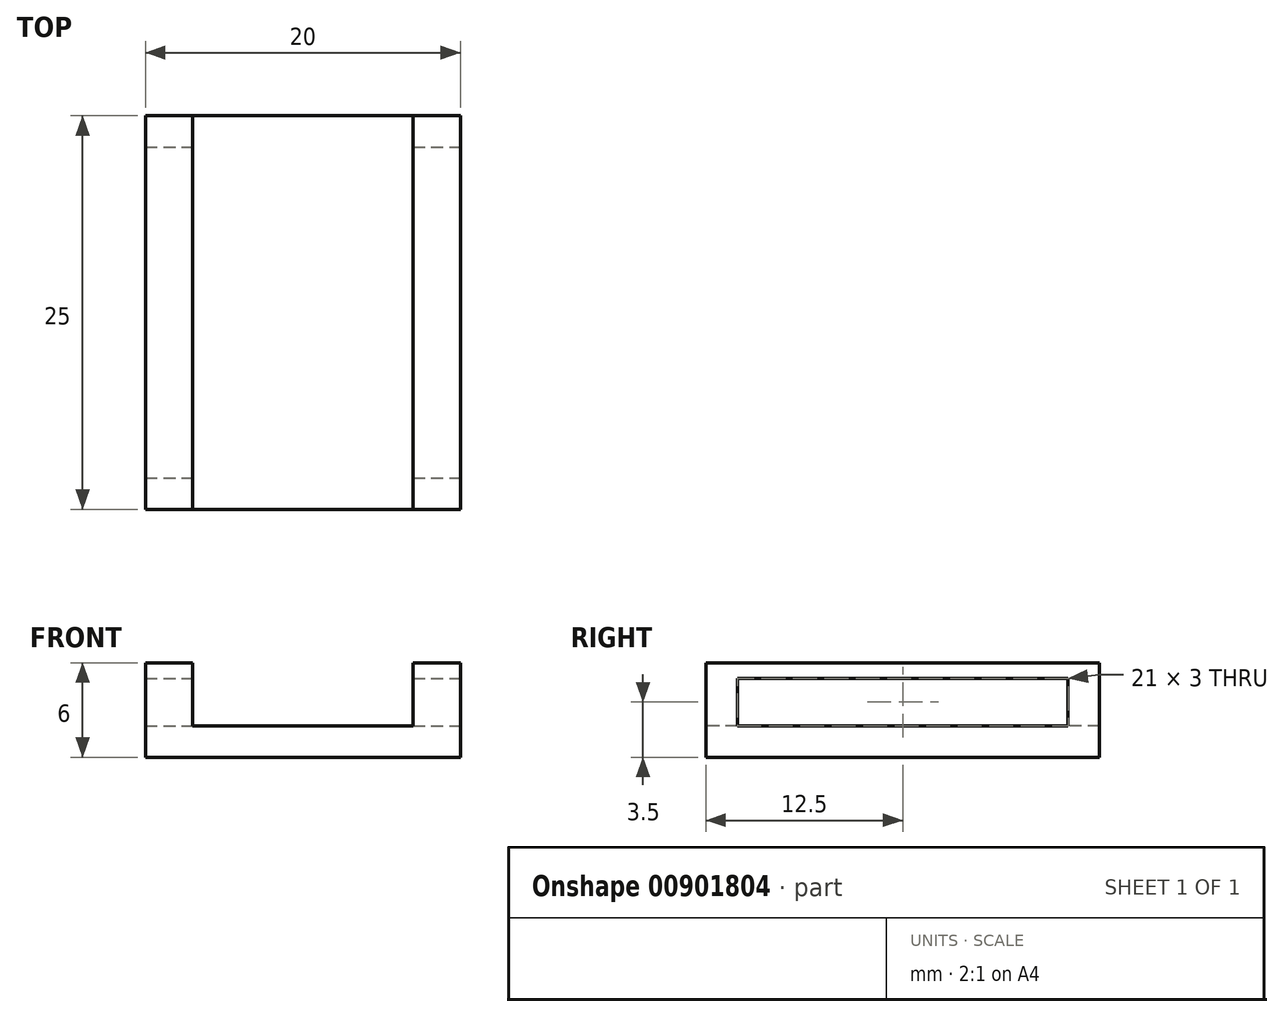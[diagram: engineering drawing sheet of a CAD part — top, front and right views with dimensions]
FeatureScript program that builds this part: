
annotation { "Feature Type Name" : "Feature", "Feature Type Description" : "" }
export const myFeature = defineFeature(function(context is Context, id is Id, definition is map)
    precondition{}
    {
        {
            var Q0;
            Q0=qCreatedBy(makeId("Top.planeOp"),FACE);
            var sketch = newSketch(context, id + "F0", { "sketchPlane" : qUnion([Q0])});
            skLineSegment(sketch, "E0.bottom", {"start": v(-10, 12.5) * mm, "end": v(10, 12.5) * mm});
            skLineSegment(sketch, "E0.top", {"start": v(-10, -12.5) * mm, "end": v(10, -12.5) * mm});
            skLineSegment(sketch, "E0.left", {"start": v(-10, 12.5) * mm, "end": v(-10, -12.5) * mm});
            skLineSegment(sketch, "E0.right", {"start": v(10, 12.5) * mm, "end": v(10, -12.5) * mm});
            skPoint(sketch, "E0.middle", {"position": v(0, 0) * mm});
            skSolve(sketch);
        }
        {
            var Q0;
            Q0=makeQuery(id+"F0.imprint","IMPRINT",FACE,{"disambiguationData":[TD([[makeQuery(id+"F0.imprint","IMPRINT",EDGE,{"derivedFrom":sQuery(id+"F0.wireOp",EDGE,"E0.bottom")}),-1.0]])]});
            extrude(context, id + "F1", {"entities" : qUnion([Q0]), "depth" : 2 * mm, "offsetDistance" : 25 * mm});
        }
        {
            var Q0;
            Q0=makeQuery(id+"F1.opExtrude","CAP_FACE",FACE,{"disambiguationData":[OSD([sQuery(id+"F0.wireOp",EDGE,"E0.bottom"),sQuery(id+"F0.wireOp",EDGE,"E0.top"),sQuery(id+"F0.wireOp",EDGE,"E0.left"),sQuery(id+"F0.wireOp",EDGE,"E0.right")])],"isStart":false});
            var sketch = newSketch(context, id + "F2", { "sketchPlane" : qUnion([Q0])});
            skLineSegment(sketch, "E1.bottom", {"start": v(-10, 12.5) * mm, "end": v(-7, 12.5) * mm});
            skLineSegment(sketch, "E1.top", {"start": v(-10, -12.5) * mm, "end": v(-7, -12.5) * mm});
            skLineSegment(sketch, "E1.left", {"start": v(-10, 12.5) * mm, "end": v(-10, -12.5) * mm});
            skLineSegment(sketch, "E1.right", {"start": v(-7, 12.5) * mm, "end": v(-7, -12.5) * mm});
            skLineSegment(sketch, "E2.bottom", {"start": v(10, 12.5) * mm, "end": v(7, 12.5) * mm});
            skLineSegment(sketch, "E2.top", {"start": v(10, -12.5) * mm, "end": v(7, -12.5) * mm});
            skLineSegment(sketch, "E2.left", {"start": v(10, 12.5) * mm, "end": v(10, -12.5) * mm});
            skLineSegment(sketch, "E2.right", {"start": v(7, 12.5) * mm, "end": v(7, -12.5) * mm});
            skSolve(sketch);
        }
        {
            var Q0;
            Q0=makeQuery(id+"F2.imprint","IMPRINT",FACE,{"disambiguationData":[TD([[makeQuery(id+"F2.imprint","IMPRINT",EDGE,{"derivedFrom":sQuery(id+"F2.wireOp",EDGE,"E1.bottom")}),-1.0]])]});
            var Q1;
            Q1=makeQuery(id+"F2.imprint","IMPRINT",FACE,{"disambiguationData":[TD([[makeQuery(id+"F2.imprint","IMPRINT",EDGE,{"derivedFrom":sQuery(id+"F2.wireOp",EDGE,"E2.bottom")}),-1.0]])]});
            extrude(context, id + "F3", {"entities" : qUnion([Q0, Q1]), "operationType" : NewBodyOperationType.ADD, "depth" : 4 * mm, "offsetDistance" : 25 * mm});
        }
        {
            var Q0;
            Q0=makeQuery(id+"F3.boolean.opBoolean","MERGE",FACE,{"derivedFrom":[makeQuery(id+"F1.opExtrude","SWEPT_FACE",FACE,{"disambiguationData":[OSD([sQuery(id+"F0.wireOp",EDGE,"E0.right")])]}),makeQuery(id+"F3.opExtrude","SWEPT_FACE",FACE,{"disambiguationData":[OSD([sQuery(id+"F2.wireOp",EDGE,"E2.left")])]})]});
            var sketch = newSketch(context, id + "F4", { "sketchPlane" : qUnion([Q0])});
            skLineSegment(sketch, "E3.bottom", {"start": v(-10.5, 5) * mm, "end": v(10.5, 5) * mm});
            skLineSegment(sketch, "E3.top", {"start": v(-10.5, 2) * mm, "end": v(10.5, 2) * mm});
            skLineSegment(sketch, "E3.left", {"start": v(-10.5, 5) * mm, "end": v(-10.5, 2) * mm});
            skLineSegment(sketch, "E3.right", {"start": v(10.5, 5) * mm, "end": v(10.5, 2) * mm});
            skSolve(sketch);
        }
        {
            var Q0;
            Q0=makeQuery(id+"F4.imprint","IMPRINT",FACE,{"disambiguationData":[TD([[makeQuery(id+"F4.imprint","IMPRINT",EDGE,{"derivedFrom":sQuery(id+"F4.wireOp",EDGE,"E3.bottom")}),-1.0]])]});
            extrude(context, id + "F5", {"entities" : qUnion([Q0]), "operationType" : NewBodyOperationType.REMOVE, "oppositeDirection" : true, "depth" : 25 * mm, "offsetDistance" : 25 * mm});
        }
    });
